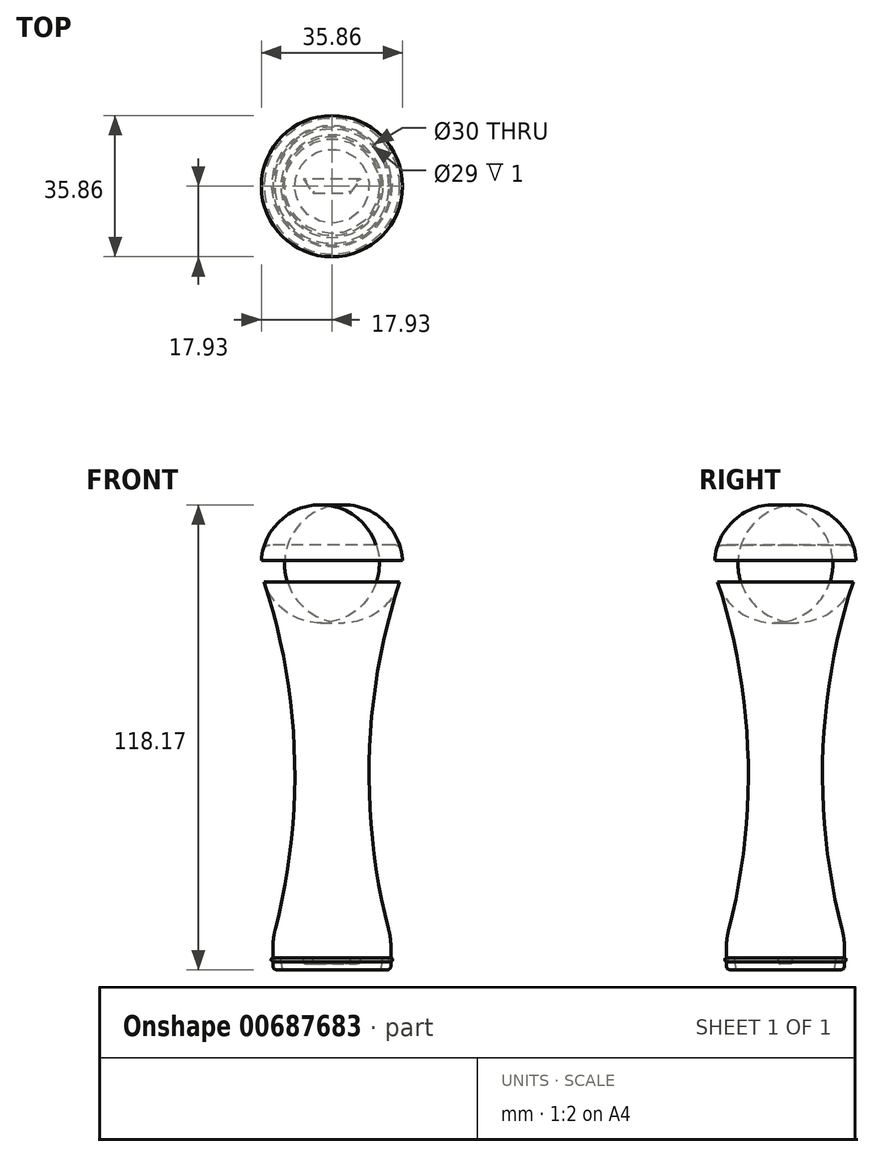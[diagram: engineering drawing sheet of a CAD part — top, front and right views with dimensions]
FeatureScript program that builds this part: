
annotation { "Feature Type Name" : "Feature", "Feature Type Description" : "" }
export const myFeature = defineFeature(function(context is Context, id is Id, definition is map)
    precondition{}
    {
        {
            var Q0;
            Q0=qCreatedBy(makeId("Front.planeOp"),FACE);
            var sketch = newSketch(context, id + "F0", { "sketchPlane" : qUnion([Q0])});
            skArc(sketch, "E0", {"start": v(-17.25, 85) * mm, "mid": v(-17.93, 81.03) * mm, "end": v(-17.7, 77) * mm});
            skLineSegment(sketch, "E1", {"start": v(0, 85) * mm, "end": v(0, 80) * mm});
            skLineSegment(sketch, "E2", {"start": v(0, 80) * mm, "end": v(0, 0) * mm});
            skLineSegment(sketch, "E3", {"start": v(0, 0) * mm, "end": v(0, 0) * mm});
            skLineSegment(sketch, "E4", {"start": v(0, -15) * mm, "end": v(0, 0) * mm});
            skLineSegment(sketch, "E5", {"start": v(-10, 40) * mm, "end": v(0, 40) * mm, "construction": true});
            skPoint(sketch, "E5.startSnap0", {"position": v(0, 40) * mm});
            skArc(sketch, "E6", {"start": v(-15, -15) * mm, "mid": v(-9.5, 31.2) * mm, "end": v(-17.7, 77) * mm});
            skPoint(sketch, "E7.startSnap0", {"position": v(0, 85) * mm});
            skLineSegment(sketch, "E8", {"start": v(-17.25, 85) * mm, "end": v(0, 85) * mm});
            skLineSegment(sketch, "E9", {"start": v(0, -15) * mm, "end": v(0, -20) * mm});
            skPoint(sketch, "E9.endSnap0", {"position": v(0, -7.5) * mm});
            skLineSegment(sketch, "E10", {"start": v(-15, -15) * mm, "end": v(-15, -20) * mm});
            skLineSegment(sketch, "E11", {"start": v(-15, -20) * mm, "end": v(-15, -23) * mm});
            skLineSegment(sketch, "E12", {"start": v(-15, -23) * mm, "end": v(-12.5, -23) * mm});
            skLineSegment(sketch, "E13", {"start": v(-12.5, -23) * mm, "end": v(-13, -20) * mm});
            skLineSegment(sketch, "E14", {"start": v(-13, -20) * mm, "end": v(0, -20) * mm});
            skSolve(sketch);
        }
        {
            var Q0;
            Q0=makeQuery(id+"F0.imprint","IMPRINT",FACE,{"disambiguationData":[TD([[makeQuery(id+"F0.imprint","IMPRINT",EDGE,{"derivedFrom":sQuery(id+"F0.wireOp",EDGE,"E0")}),1.0]])]});
            var Q1;
            Q1=sQuery(id+"F0.wireOp",EDGE,"E4");
            revolve(context, id + "F1", {"entities" : qUnion([Q0]), "axis" : qUnion([Q1]), "revolveType" : RevolveType.FULL});
        }
        {
            var Q0;
            Q0=makeQuery(id+"F1.opRevolve","SWEPT_EDGE",EDGE,{"disambiguationData":[OSD([sQuery(id+"F0.wireOp",EDGE,"E0"),sQuery(id+"F0.wireOp",EDGE,"E8")])]});
            fillet(context, id + "F2", {"entities" : qUnion([Q0]), "radius" : 2 * mm, "tangentPropagation" : true, "allowEdgeOverflow" : false});
        }
        {
            var Q0;
            Q0=makeQuery(id+"F1.opRevolve","SWEPT_EDGE",EDGE,{"disambiguationData":[OSD([sQuery(id+"F0.wireOp",EDGE,"E6"),sQuery(id+"F0.wireOp",EDGE,"E10")])]});
            fillet(context, id + "F3", {"entities" : qUnion([Q0]), "radius" : 20 * mm, "tangentPropagation" : true, "allowEdgeOverflow" : false});
        }
        {
            var Q0;
            Q0=makeQuery(id+"F1.opRevolve","SWEPT_FACE",FACE,{"disambiguationData":[OSD([sQuery(id+"F0.wireOp",EDGE,"E14")])]});
            var sketch = newSketch(context, id + "F4", { "sketchPlane" : qUnion([Q0])});
            skPoint(sketch, "E15.middle", {"position": v(0, 0) * mm});
            skSolve(sketch);
        }
        {
            var Q0;
            Q0=makeQuery(id+"F1.opRevolve","SWEPT_EDGE",EDGE,{"disambiguationData":[OSD([sQuery(id+"F0.wireOp",EDGE,"E11"),sQuery(id+"F0.wireOp",EDGE,"E12")])]});
            fillet(context, id + "F5", {"entities" : qUnion([Q0]), "radius" : 1 * mm, "tangentPropagation" : true, "allowEdgeOverflow" : false});
        }
        {
            var Q0;
            Q0=makeQuery(id+"F4.imprint","IMPRINT",FACE,{"disambiguationData":[TD([[makeQuery(id+"F4.imprint","IMPRINT",EDGE,{"derivedFrom":makeQuery(id+"F1.opRevolve","SWEPT_EDGE",EDGE,{"disambiguationData":[OSD([sQuery(id+"F0.wireOp",EDGE,"E13"),sQuery(id+"F0.wireOp",EDGE,"E14")])]})}),1.0]])]});
            var sketch = newSketch(context, id + "F6", { "sketchPlane" : qUnion([Q0])});
            skCircle(sketch, "E16", {"center": v(0, 0) * mm, "radius": 14.5 * mm});
            skCircle(sketch, "E17.0", {"center": v(0, 0) * mm, "radius": 15.5 * mm});
            skSolve(sketch);
        }
        {
            var Q0;
            Q0 = qSketchRegion(id + "F6", true);
            extrude(context, id + "F7", {"entities" : qUnion([Q0]), "depth" : 1 * mm, "offsetDistance" : 25 * mm});
        }
        {
            var Q0;
            Q0=makeQuery(id+"F7.opExtrude","CAP_EDGE",EDGE,{"disambiguationData":[OSD([sQuery(id+"F6.wireOp",EDGE,"E17.0")])],"isStart":true});
            fillet(context, id + "F8", {"entities" : qUnion([Q0]), "radius" : 0.5 * mm, "tangentPropagation" : true, "allowEdgeOverflow" : false});
        }
        {
            var Q0;
            Q0=makeQuery(id+"F7.opExtrude","CAP_EDGE",EDGE,{"disambiguationData":[OSD([sQuery(id+"F6.wireOp",EDGE,"E17.0")])],"isStart":false});
            chamfer(context, id + "F9", {"entities" : qUnion([Q0]), "width" : 0.5 * mm, "tangentPropagation" : true});
        }
        {
            var Q0;
            {var subQ0=sQuery(id+"F6.wireOp",EDGE,"E17.0");Q0=makeQuery(id+"F9.opChamfer","BLEND_EDGE",EDGE,{"blendedFrom":[makeQuery(id+"F7.opExtrude","CAP_EDGE",EDGE,{"disambiguationData":[OSD([subQ0])],"isStart":false}),makeQuery(id+"F8.opFillet","BLEND_FACE",FACE,{"disambiguationData":[OSD([subQ0])]})],"blendedInto":[makeQuery(id+"F8.opFillet","BLEND_FACE",FACE,{"disambiguationData":[OSD([subQ0])]})]});}
            fillet(context, id + "F10", {"entities" : qUnion([Q0]), "radius" : 0.4 * mm, "tangentPropagation" : true, "allowEdgeOverflow" : false});
        }
        {
            var Q0;
            Q0=makeQuery(id+"F4.imprint","IMPRINT",FACE,{"disambiguationData":[TD([[makeQuery(id+"F4.imprint","IMPRINT",EDGE,{"derivedFrom":makeQuery(id+"F1.opRevolve","SWEPT_EDGE",EDGE,{"disambiguationData":[OSD([sQuery(id+"F0.wireOp",EDGE,"E13"),sQuery(id+"F0.wireOp",EDGE,"E14")])]})}),1.0]])]});
            var sketch = newSketch(context, id + "F11", { "sketchPlane" : qUnion([Q0])});
            skLineSegment(sketch, "E18", {"start": v(7.25, -1.75) * mm, "end": v(-7.25, -1.75) * mm});
            skLineSegment(sketch, "E19", {"start": v(-7.25, -1.75) * mm, "end": v(-4.75, 1.75) * mm});
            skLineSegment(sketch, "E20", {"start": v(-4.75, 1.75) * mm, "end": v(4.75, 1.75) * mm});
            skLineSegment(sketch, "E21", {"start": v(4.75, 1.75) * mm, "end": v(7.25, -1.75) * mm});
            skLineSegment(sketch, "E22", {"start": v(0, 1.75) * mm, "end": v(0, 0) * mm, "construction": true});
            skLineSegment(sketch, "E23", {"start": v(0, 0) * mm, "end": v(0, -1.75) * mm, "construction": true});
            skSolve(sketch);
        }
        {
            var Q0;
            Q0=makeQuery(id+"F11.imprint","IMPRINT",FACE,{"disambiguationData":[TD([[makeQuery(id+"F11.imprint","IMPRINT",EDGE,{"derivedFrom":sQuery(id+"F11.wireOp",EDGE,"E18")}),-1.0]])]});
            extrude(context, id + "F12", {"entities" : qUnion([Q0]), "operationType" : NewBodyOperationType.ADD, "depth" : 1.5 * mm, "offsetDistance" : 25 * mm});
        }
        {
            var Q0;
            Q0=makeQuery(id+"F12.opExtrude","CAP_FACE",FACE,{"disambiguationData":[OSD([sQuery(id+"F11.wireOp",EDGE,"E18"),sQuery(id+"F11.wireOp",EDGE,"E19"),sQuery(id+"F11.wireOp",EDGE,"E20"),sQuery(id+"F11.wireOp",EDGE,"E21")])],"isStart":false});
            fillet(context, id + "F13", {"entities" : qUnion([Q0]), "radius" : 0.5 * mm, "tangentPropagation" : true, "allowEdgeOverflow" : false});
        }
        {
            var Q0;
            Q0=makeQuery(id+"F1.opRevolve","SWEPT_EDGE",EDGE,{"disambiguationData":[OSD([sQuery(id+"F0.wireOp",EDGE,"E0"),sQuery(id+"F0.wireOp",EDGE,"E6")])]});
            fillet(context, id + "F14", {"entities" : qUnion([Q0]), "radius" : 15 * mm, "tangentPropagation" : true, "allowEdgeOverflow" : false});
        }
    });
